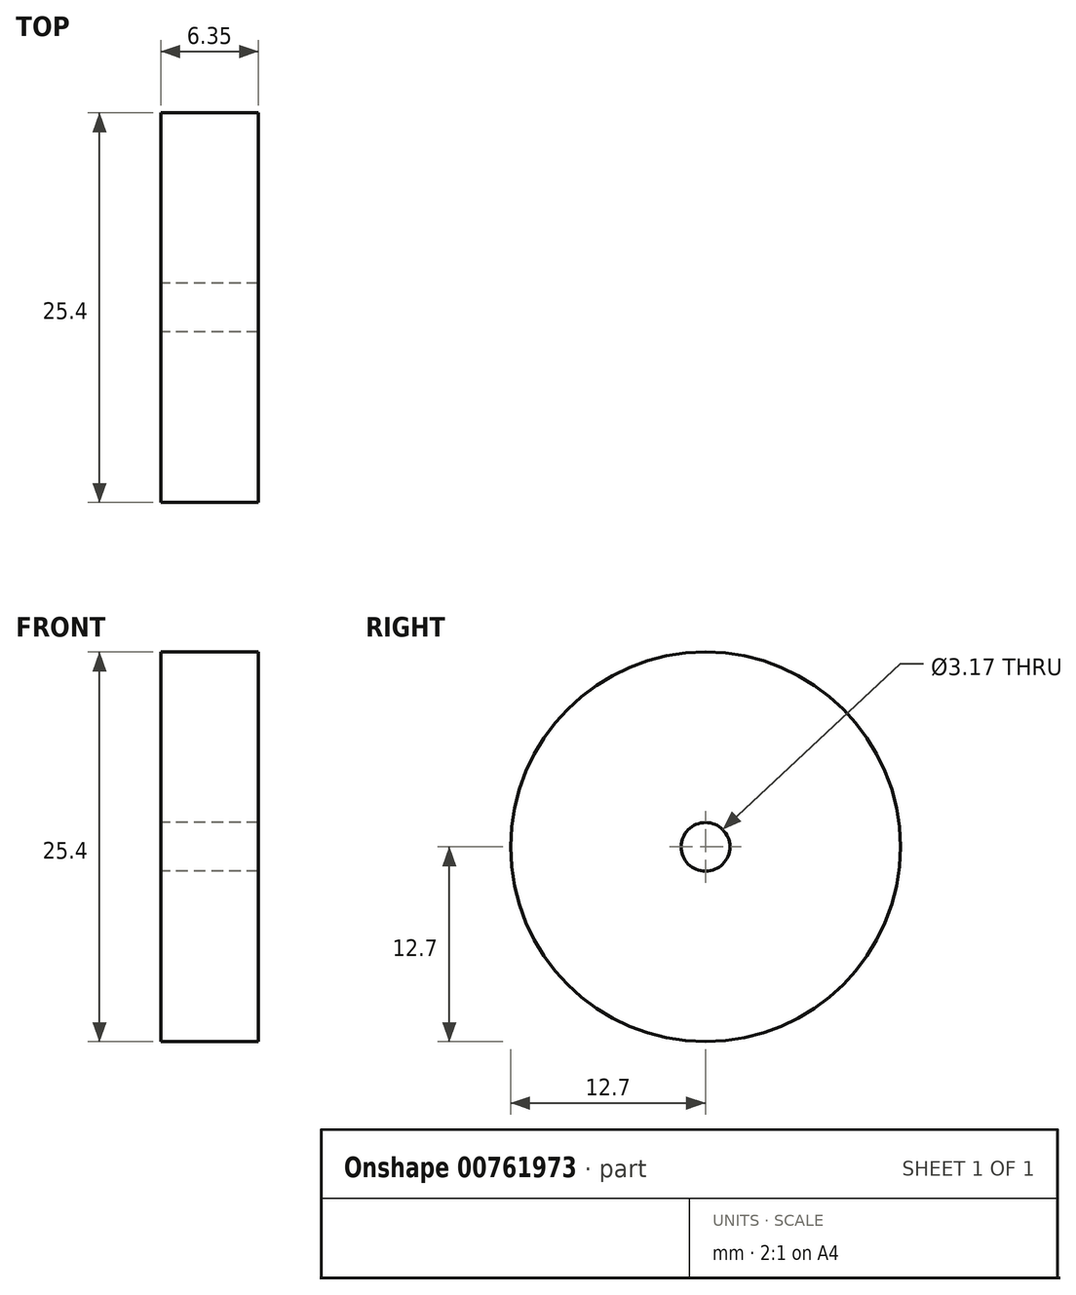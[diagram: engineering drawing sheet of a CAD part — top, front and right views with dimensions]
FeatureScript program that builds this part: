
annotation { "Feature Type Name" : "Feature", "Feature Type Description" : "" }
export const myFeature = defineFeature(function(context is Context, id is Id, definition is map)
    precondition{}
    {
        {
            var Q0;
            Q0=qCreatedBy(makeId("Right.planeOp"),FACE);
            var sketch = newSketch(context, id + "F0", { "sketchPlane" : qUnion([Q0])});
            skCircle(sketch, "E0", {"center": v(0, 0) * mm, "radius": 12.7 * mm});
            skCircle(sketch, "E1", {"center": v(0, 0) * mm, "radius": 1.59 * mm});
            skSolve(sketch);
        }
        {
            var Q0;
            Q0=makeQuery(id+"F0.imprint","IMPRINT",FACE,{"disambiguationData":[TD([[makeQuery(id+"F0.imprint","IMPRINT",EDGE,{"derivedFrom":sQuery(id+"F0.wireOp",EDGE,"E0")}),1.0]])]});
            extrude(context, id + "F1", {"entities" : qUnion([Q0]), "depth" : 6.35 * mm, "offsetDistance" : 25.4 * mm});
        }
    });
